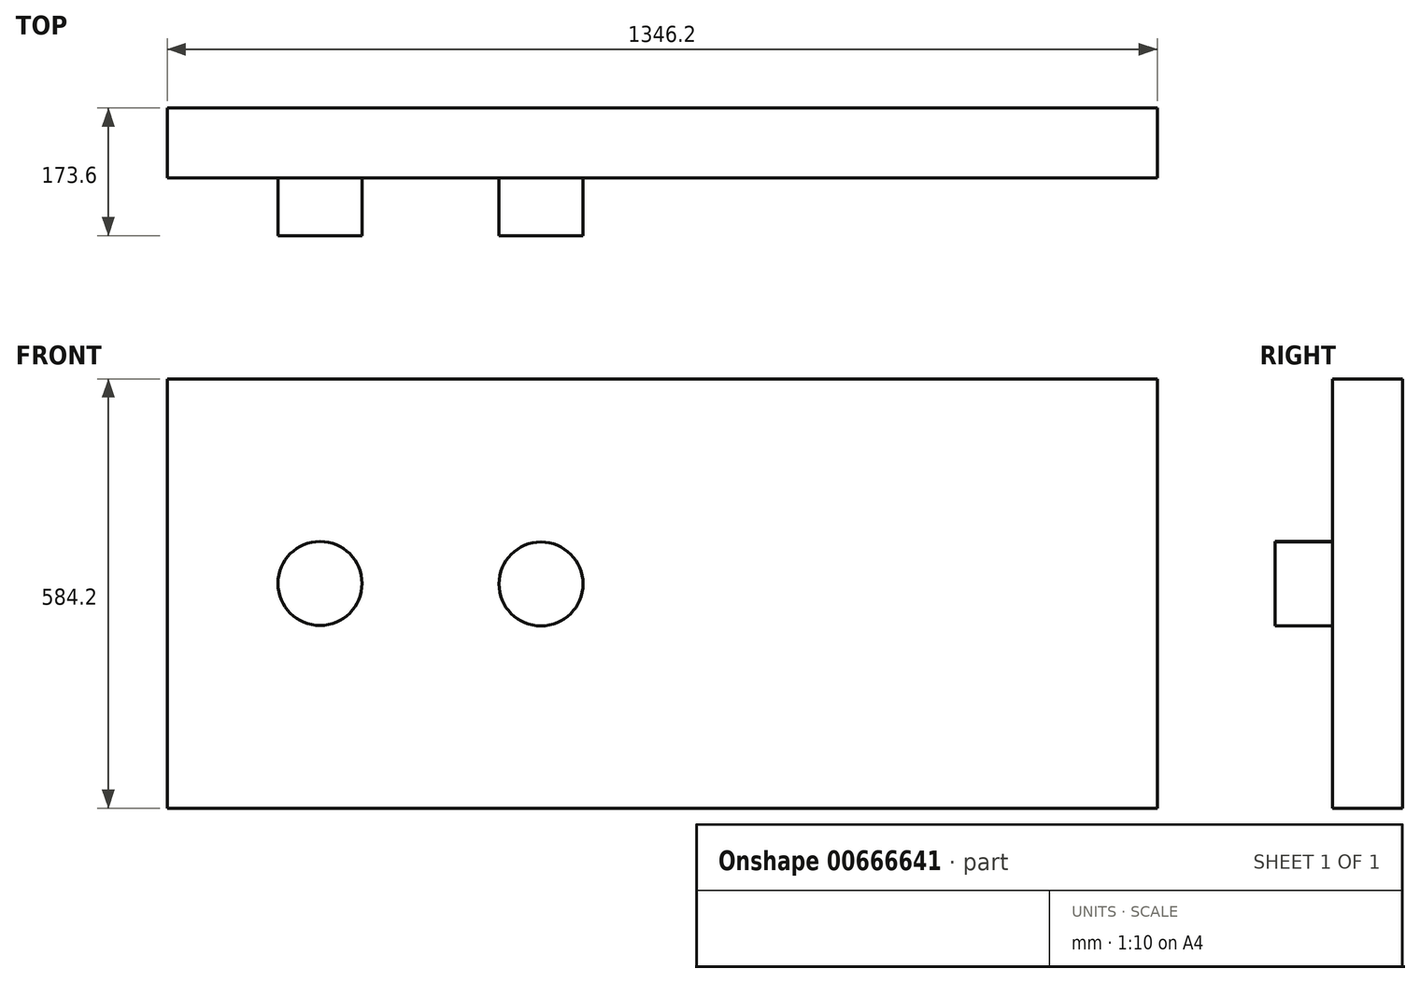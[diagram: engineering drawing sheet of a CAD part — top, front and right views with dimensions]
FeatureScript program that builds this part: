
annotation { "Feature Type Name" : "Feature", "Feature Type Description" : "" }
export const myFeature = defineFeature(function(context is Context, id is Id, definition is map)
    precondition{}
    {
        {
            var Q0;
            Q0=qCreatedBy(makeId("Front.planeOp"),FACE);
            var sketch = newSketch(context, id + "F0", { "sketchPlane" : qUnion([Q0])});
            skLineSegment(sketch, "E0.bottom", {"start": v(-683.52, 75.97) * mm, "end": v(662.68, 75.97) * mm});
            skLineSegment(sketch, "E0.top", {"start": v(-683.52, -508.23) * mm, "end": v(662.68, -508.23) * mm});
            skLineSegment(sketch, "E0.left", {"start": v(-683.52, 75.97) * mm, "end": v(-683.52, -508.23) * mm});
            skLineSegment(sketch, "E0.right", {"start": v(662.68, 75.97) * mm, "end": v(662.68, -508.23) * mm});
            skLineSegment(sketch, "E1.bottom", {"start": v(262.35, -508.23) * mm, "end": v(268.24, -508.23) * mm});
            skLineSegment(sketch, "E1.top", {"start": v(262.35, -508.23) * mm, "end": v(268.24, -508.23) * mm});
            skLineSegment(sketch, "E1.left", {"start": v(262.35, -508.23) * mm, "end": v(262.35, -508.23) * mm});
            skLineSegment(sketch, "E1.right", {"start": v(268.24, -508.23) * mm, "end": v(268.24, -508.23) * mm});
            skCircle(sketch, "E2", {"center": v(-475.63, -202.37) * mm, "radius": 57.15 * mm});
            skLineSegment(sketch, "E3", {"start": v(-475.63, -202.37) * mm, "end": v(-134.25, -202.37) * mm});
            skCircle(sketch, "E4", {"center": v(-134.25, -202.37) * mm, "radius": 57.15 * mm});
            skSolve(sketch);
        }
        {
            var Q0;
            Q0=makeQuery(id+"F0.imprint","IMPRINT",FACE,{"disambiguationData":[TD([[makeQuery(id+"F0.imprint","IMPRINT",EDGE,{"derivedFrom":sQuery(id+"F0.wireOp",EDGE,"E0.bottom")}),-1.0]])]});
            var Q1;
            Q1=makeQuery(id+"F0.imprint","IMPRINT",FACE,{"disambiguationData":[TD([[makeQuery(id+"F0.imprint","IMPRINT",EDGE,{"derivedFrom":sQuery(id+"F0.wireOp",EDGE,"E2")}),1.0]])]});
            var Q2;
            Q2=makeQuery(id+"F0.imprint","IMPRINT",FACE,{"disambiguationData":[TD([[makeQuery(id+"F0.imprint","IMPRINT",EDGE,{"derivedFrom":sQuery(id+"F0.wireOp",EDGE,"E4")}),1.0]])]});
            extrude(context, id + "F1", {"entities" : qUnion([Q0, Q1, Q2]), "depth" : 95.2 * mm, "offsetDistance" : 25.4 * mm});
        }
        {
            var Q0;
            Q0=qCreatedBy(makeId("Front.planeOp"),FACE);
            var sketch = newSketch(context, id + "F2", { "sketchPlane" : qUnion([Q0])});
            skCircle(sketch, "E5", {"center": v(-175.21, -203.1) * mm, "radius": 57.15 * mm});
            skSolve(sketch);
        }
        {
            var Q0;
            Q0 = qSketchRegion(id + "F2", true);
            var Q1;
            Q1=makeQuery(id+"F0.imprint","IMPRINT",FACE,{"disambiguationData":[TD([[makeQuery(id+"F0.imprint","IMPRINT",EDGE,{"derivedFrom":sQuery(id+"F0.wireOp",EDGE,"E2")}),1.0]])]});
            extrude(context, id + "F3", {"entities" : qUnion([Q0, Q1]), "operationType" : NewBodyOperationType.ADD, "depth" : 173.6 * mm, "offsetDistance" : 25.4 * mm});
        }
    });
